# Revit family: SL31
name_source: partatom
category: Plumbing Fixtures
revit_build: Autodesk Revit 2015 (Build: 20140606_1530(x64)
units: mm (PartAtom-declared; Revit-internal decimal feet)

## types (5) — shared parameters
Aluminium = Aluminum - Polished
Chrome = Chrome - Polished
Glass = Glass
Manufacturer = SanSwiss
Model = SLT31
Seal = Seal
URL = http://www.sanswiss.com

## per-type parameters (varying)
| type | A | B | C | E |
| 900 | 900 mm  [stored 2.95276 ft] | 634 mm  [stored 2.08005 ft] | 266 mm | 200 mm  [stored 0.656168 ft] |
| 1000 | 1000 mm  [stored 3.28084 ft] | 634 mm  [stored 2.08005 ft] | 366 mm | 235 mm  [stored 0.770997 ft] |
| 1200 | 1200 mm | 834 mm  [stored 2.73622 ft] | 366 mm | 235 mm  [stored 0.770997 ft] |
| 800 | 800 mm  [stored 2.62467 ft] | 534 mm  [stored 1.75197 ft] | 266 mm | 200 mm  [stored 0.656168 ft] |
| 1400 | 1400 mm  [stored 4.59318 ft] | 934 mm  [stored 3.0643 ft] | 466 mm | 267 mm  [stored 0.875984 ft] |

note: [stored X ft] marks values corroborated as IEEE doubles in the binary element streams (Revit-internal decimal feet)

## geometry (parser evidence)
native form markers: Sweep x16
no freeform markers — native parametric forms only
